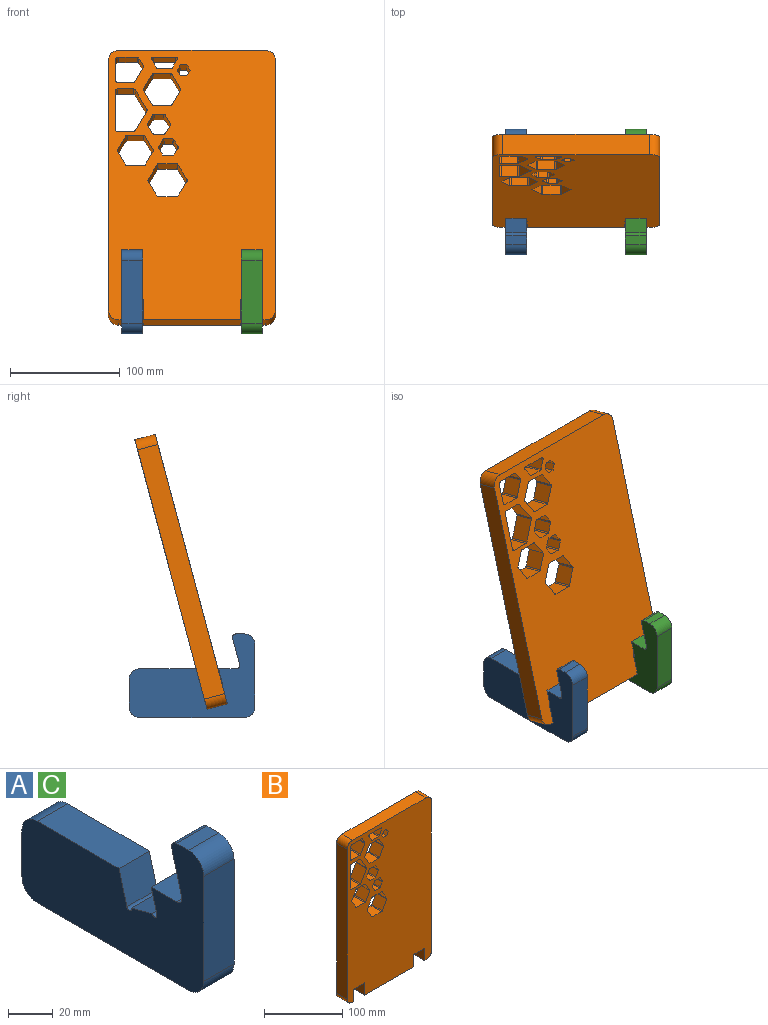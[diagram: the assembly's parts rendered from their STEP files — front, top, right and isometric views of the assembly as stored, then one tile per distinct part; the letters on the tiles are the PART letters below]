
ASSEMBLY  parts=3 mates=6
PART A: 20 faces, bbox 19.1x114.3x76.2 mm
  f0: plane 19.05x16.18mm, normal (0,0,1), area 308.3mm2, adj f7,f8,f17,f18
  f1: plane 95.25x19.05mm, normal (0,0,-1), area 1814.5mm2, adj f7,f8,f9,f12
  f2: plane 25.4x19.05mm, normal (0,1,0), area 483.9mm2, adj f7,f8,f9,f10
  f3: plane 51.51x19.05mm, normal (0,0,1), area 981.2mm2, adj f7,f8,f10,f13
  f4: plane 23.76x19.05mm, normal (0,0.97,-0.26), area 468.5mm2, adj f7,f8,f18,f19
  f5: plane 19.05x7.54mm, normal (0,0,1), area 143.7mm2, adj f7,f8,f11,f19
  f6: plane 57.15x19.05mm, normal (0,-1,0), area 1088.7mm2, adj f7,f8,f11,f12
  f7: plane 114.3x76.2mm, normal (1,0,0), area 5211.8mm2, adj f0,f1,f2,f3,f4,f5,f6,f9
  f8: plane 114.3x76.2mm, normal (-1,0,0), area 5211.8mm2, adj f0,f1,f2,f3,f4,f5,f6,f9
  f9: cylinder r=9.53mm len=19.05mm, axis (-1,0,0), area 285mm2, adj f1,f2,f7,f8
  f10: cylinder r=9.53mm len=19.05mm, axis (1,0,0), area 285mm2, adj f2,f3,f7,f8
  f11: cylinder r=9.53mm len=19.05mm, axis (1,0,0), area 285mm2, adj f5,f6,f7,f8
  f12: cylinder r=9.53mm len=19.05mm, axis (1,0,0), area 285mm2, adj f1,f6,f7,f8
  f13: plane 19.05x18.4mm, normal (0,-0.97,0.26), area 362.9mm2, adj f3,f7,f8,f14
  f14: cylinder r=1.59mm len=19.05mm, axis (-1,0,0), area 95mm2, adj f7,f8,f13,f15
  f15: plane 19.05x12.76mm, normal (0,0.26,0.97), area 251.6mm2, adj f7,f8,f14,f16
  f16: cylinder r=1.59mm len=19.05mm, axis (-1,0,0), area 95mm2, adj f7,f8,f15,f17
  f17: plane 19.05x13.34mm, normal (0,0.97,-0.26), area 263.1mm2, adj f0,f7,f8,f16
  f18: cylinder r=3.17mm len=19.05mm, axis (1,0,0), area 110.8mm2, adj f0,f4,f7,f8
  f19: cylinder r=3.17mm len=19.05mm, axis (1,0,0), area 110.8mm2, adj f4,f5,f7,f8
PART B: 115 faces, bbox 152.4x19.1x254 mm
  f0: plane 254x152.4mm, normal (0,-1,0), area 33243.4mm2, adj f2,f3,f4,f5,f6,f7,f8,f9
  f1: plane 254x152.4mm, normal (0,1,0), area 33243.4mm2, adj f2,f3,f4,f5,f6,f7,f8,f9
  f2: plane 88.9x19.05mm, normal (0,0,-1), area 1693.5mm2, adj f0,f1,f8,f15
  f3: plane 19.05x2.67mm, normal (0,0,-1), area 50.8mm2, adj f0,f1,f9,f19
  f4: plane 234.95x19.05mm, normal (-1,0,0), area 4475.8mm2, adj f0,f1,f18,f21
  f5: plane 19.05x2.67mm, normal (0,0,-1), area 50.8mm2, adj f0,f1,f14,f18
  f6: plane 234.95x19.05mm, normal (1,0,0), area 4475.8mm2, adj f0,f1,f19,f20
  f7: plane 133.35x19.05mm, normal (0,0,1), area 2540.3mm2, adj f0,f1,f20,f21
  f8: plane 19.05x19.05mm, normal (1,0,0), area 362.9mm2, adj f0,f1,f2,f12
  f9: plane 19.05x19.05mm, normal (-1,0,0), area 362.9mm2, adj f0,f1,f3,f10
  f10: cylinder r=0.79mm len=19.05mm, axis (0,-1,0), area 47.5mm2, adj f0,f1,f9,f11
  f11: plane 19.05x16.38mm, normal (0,0,-1), area 312.1mm2, adj f0,f1,f10,f12
  f12: cylinder r=0.79mm len=19.05mm, axis (0,-1,0), area 47.5mm2, adj f0,f1,f8,f11
  f13: cylinder r=0.79mm len=19.05mm, axis (0,-1,0), area 47.5mm2, adj f0,f1,f14,f17
  f14: plane 19.05x19.05mm, normal (1,0,0), area 362.9mm2, adj f0,f1,f5,f13
  f15: plane 19.05x19.05mm, normal (-1,0,0), area 362.9mm2, adj f0,f1,f2,f16
  f16: cylinder r=0.79mm len=19.05mm, axis (0,-1,0), area 47.5mm2, adj f0,f1,f15,f17
  f17: plane 19.05x16.38mm, normal (0,0,-1), area 312.1mm2, adj f0,f1,f13,f16
  f18: cylinder r=9.53mm len=19.05mm, axis (0,-1,0), area 285mm2, adj f0,f1,f4,f5
  f19: cylinder r=9.53mm len=19.05mm, axis (0,1,0), area 285mm2, adj f0,f1,f3,f6
  f20: cylinder r=9.53mm len=19.05mm, axis (0,-1,0), area 285mm2, adj f0,f1,f6,f7
  f21: cylinder r=9.53mm len=19.05mm, axis (0,1,0), area 285mm2, adj f0,f1,f4,f7
  f22: plane 19.05x16.92mm, normal (0,0,-1), area 322.4mm2, adj f0,f1,f23,f111
  f23: cylinder r=3.17mm len=19.05mm, axis (0,-1,0), area 95mm2, adj f0,f1,f22,f24
  f24: plane 19.05x18.94mm, normal (1,0,0), area 360.7mm2, adj f0,f1,f23,f114
  f25: plane 19.05x14.84mm, normal (0,0,1), area 282.8mm2, adj f0,f1,f113,f114
  f26: plane 19.05x13.44mm, normal (-0.87,0,0.5), area 295.6mm2, adj f0,f1,f112,f113
  f27: plane 19.05x7.09mm, normal (-0.87,0,-0.5), area 155.9mm2, adj f0,f1,f111,f112
  f28: plane 20.32x19.05mm, normal (0,0,-1), area 387.2mm2, adj f0,f1,f73,f76
  f29: plane 19.05x8.01mm, normal (0.87,0,0.5), area 176.1mm2, adj f0,f1,f75,f76
  f30: plane 19.05x11.08mm, normal (0,0,1), area 211mm2, adj f0,f1,f74,f75
  f31: plane 19.05x8.01mm, normal (-0.87,0,0.5), area 176.1mm2, adj f0,f1,f73,f74
  f32: plane 19.05x5.13mm, normal (0.87,0,0.5), area 112.8mm2, adj f0,f1,f33,f37
  f33: plane 19.05x5.92mm, normal (0,0,1), area 112.8mm2, adj f0,f1,f32,f34
  f34: plane 19.05x5.13mm, normal (-0.87,0,0.5), area 112.8mm2, adj f0,f1,f33,f35
  f35: plane 19.05x5.13mm, normal (-0.87,0,-0.5), area 112.8mm2, adj f0,f1,f34,f36
  f36: plane 19.05x5.92mm, normal (0,0,-1), area 112.8mm2, adj f0,f1,f35,f37
  f37: plane 19.05x5.13mm, normal (0.87,0,-0.5), area 112.8mm2, adj f0,f1,f32,f36
  f38: plane 19.05x6.4mm, normal (-0.87,0,-0.5), area 140.9mm2, adj f0,f1,f77,f82
  f39: plane 19.05x7.4mm, normal (0,0,-1), area 140.9mm2, adj f0,f1,f81,f82
  f40: plane 19.05x6.4mm, normal (0.87,0,-0.5), area 140.9mm2, adj f0,f1,f80,f81
  f41: plane 19.05x6.4mm, normal (0.87,0,0.5), area 140.9mm2, adj f0,f1,f79,f80
  f42: plane 19.05x7.4mm, normal (0,0,1), area 140.9mm2, adj f0,f1,f78,f79
  f43: plane 19.05x6.4mm, normal (-0.87,0,0.5), area 140.9mm2, adj f0,f1,f77,f78
  f44: plane 19.05x14.08mm, normal (-0.87,0,-0.5), area 309.6mm2, adj f0,f1,f83,f88
  f45: plane 19.05x16.25mm, normal (0,0,-1), area 309.6mm2, adj f0,f1,f87,f88
  f46: plane 19.05x14.08mm, normal (0.87,0,-0.5), area 309.6mm2, adj f0,f1,f86,f87
  f47: plane 19.05x14.08mm, normal (0.87,0,0.5), area 309.6mm2, adj f0,f1,f85,f86
  f48: plane 19.05x16.25mm, normal (0,0,1), area 309.6mm2, adj f0,f1,f84,f85
  f49: plane 19.05x14.08mm, normal (-0.87,0,0.5), area 309.6mm2, adj f0,f1,f83,f84
  f50: plane 36.8x19.05mm, normal (1,0,0), area 701.1mm2, adj f0,f1,f100,f104
  f51: plane 19.05x15.17mm, normal (0,0,1), area 289mm2, adj f0,f1,f103,f104
  f52: plane 19.05x18.4mm, normal (-0.87,0,0.5), area 404.8mm2, adj f0,f1,f102,f103
  f53: plane 19.05x18.4mm, normal (-0.87,0,-0.5), area 404.8mm2, adj f0,f1,f101,f102
  f54: plane 19.05x15.17mm, normal (0,0,-1), area 289mm2, adj f0,f1,f100,f101
  f55: plane 19.05x13.44mm, normal (-0.87,0,-0.5), area 295.6mm2, adj f0,f1,f105,f110
  f56: plane 19.05x15.52mm, normal (0,0,-1), area 295.6mm2, adj f0,f1,f105,f106
  f57: plane 19.05x13.44mm, normal (0.87,0,-0.5), area 295.6mm2, adj f0,f1,f106,f107
  f58: plane 19.05x13.44mm, normal (0.87,0,0.5), area 295.6mm2, adj f0,f1,f107,f108
  f59: plane 19.05x15.52mm, normal (0,0,1), area 295.6mm2, adj f0,f1,f108,f109
  f60: plane 19.05x13.44mm, normal (-0.87,0,0.5), area 295.6mm2, adj f0,f1,f109,f110
  f61: plane 19.05x7.74mm, normal (-0.87,0,-0.5), area 170.2mm2, adj f0,f1,f94,f99
  f62: plane 19.05x8.94mm, normal (0,0,-1), area 170.2mm2, adj f0,f1,f98,f99
  f63: plane 19.05x7.74mm, normal (0.87,0,-0.5), area 170.2mm2, adj f0,f1,f97,f98
  f64: plane 19.05x7.74mm, normal (0.87,0,0.5), area 170.2mm2, adj f0,f1,f96,f97
  f65: plane 19.05x8.94mm, normal (0,0,1), area 170.2mm2, adj f0,f1,f95,f96
  f66: plane 19.05x7.74mm, normal (-0.87,0,0.5), area 170.2mm2, adj f0,f1,f94,f95
  f67: plane 19.05x13.65mm, normal (-0.87,0,-0.5), area 300.1mm2, adj f0,f1,f72,f93
  f68: plane 19.05x14.84mm, normal (0,0,-1), area 282.7mm2, adj f0,f1,f92,f93
  f69: plane 19.05x12.85mm, normal (0.87,0,-0.5), area 282.7mm2, adj f0,f1,f91,f92
  f70: plane 19.05x12.85mm, normal (0.87,0,0.5), area 282.7mm2, adj f0,f1,f90,f91
  f71: plane 19.05x14.84mm, normal (0,0,1), area 282.7mm2, adj f0,f1,f89,f90
  f72: plane 19.05x13.65mm, normal (-0.87,0,0.5), area 300.1mm2, adj f0,f1,f67,f89
  f73: cylinder r=1.59mm len=19.05mm, axis (0,-1,0), area 63.3mm2, adj f0,f1,f28,f31
  f74: cylinder r=1.59mm len=19.05mm, axis (0,1,0), area 31.7mm2, adj f0,f1,f30,f31
  f75: cylinder r=1.59mm len=19.05mm, axis (0,1,0), area 31.7mm2, adj f0,f1,f29,f30
  f76: cylinder r=1.59mm len=19.05mm, axis (0,-1,0), area 63.3mm2, adj f0,f1,f28,f29
  f77: cylinder r=1.59mm len=19.05mm, axis (0,1,0), area 31.7mm2, adj f0,f1,f38,f43
  f78: cylinder r=1.59mm len=19.05mm, axis (0,1,0), area 31.7mm2, adj f0,f1,f42,f43
  f79: cylinder r=1.59mm len=19.05mm, axis (0,1,0), area 31.7mm2, adj f0,f1,f41,f42
  f80: cylinder r=1.59mm len=19.05mm, axis (0,1,0), area 31.7mm2, adj f0,f1,f40,f41
  f81: cylinder r=1.59mm len=19.05mm, axis (0,1,0), area 31.7mm2, adj f0,f1,f39,f40
  f82: cylinder r=1.59mm len=19.05mm, axis (0,1,0), area 31.7mm2, adj f0,f1,f38,f39
  f83: cylinder r=1.59mm len=19.05mm, axis (0,1,0), area 31.7mm2, adj f0,f1,f44,f49
  f84: cylinder r=1.59mm len=19.05mm, axis (0,1,0), area 31.7mm2, adj f0,f1,f48,f49
  f85: cylinder r=1.59mm len=19.05mm, axis (0,1,0), area 31.7mm2, adj f0,f1,f47,f48
  f86: cylinder r=1.59mm len=19.05mm, axis (0,1,0), area 31.7mm2, adj f0,f1,f46,f47
  f87: cylinder r=1.59mm len=19.05mm, axis (0,1,0), area 31.7mm2, adj f0,f1,f45,f46
  f88: cylinder r=1.59mm len=19.05mm, axis (0,1,0), area 31.7mm2, adj f0,f1,f44,f45
  f89: cylinder r=1.59mm len=19.05mm, axis (0,1,0), area 31.7mm2, adj f0,f1,f71,f72
  f90: cylinder r=1.59mm len=19.05mm, axis (0,1,0), area 31.7mm2, adj f0,f1,f70,f71
  f91: cylinder r=1.59mm len=19.05mm, axis (0,1,0), area 31.7mm2, adj f0,f1,f69,f70
  f92: cylinder r=1.59mm len=19.05mm, axis (0,1,0), area 31.7mm2, adj f0,f1,f68,f69
  f93: cylinder r=1.59mm len=19.05mm, axis (0,1,0), area 31.7mm2, adj f0,f1,f67,f68
  f94: cylinder r=1.59mm len=19.05mm, axis (0,1,0), area 31.7mm2, adj f0,f1,f61,f66
  f95: cylinder r=1.59mm len=19.05mm, axis (0,1,0), area 31.7mm2, adj f0,f1,f65,f66
  f96: cylinder r=1.59mm len=19.05mm, axis (0,1,0), area 31.7mm2, adj f0,f1,f64,f65
  f97: cylinder r=1.59mm len=19.05mm, axis (0,1,0), area 31.7mm2, adj f0,f1,f63,f64
  f98: cylinder r=1.59mm len=19.05mm, axis (0,1,0), area 31.7mm2, adj f0,f1,f62,f63
  f99: cylinder r=1.59mm len=19.05mm, axis (0,1,0), area 31.7mm2, adj f0,f1,f61,f62
  f100: cylinder r=1.59mm len=19.05mm, axis (0,-1,0), area 47.5mm2, adj f0,f1,f50,f54
  f101: cylinder r=1.59mm len=19.05mm, axis (0,1,0), area 31.7mm2, adj f0,f1,f53,f54
  f102: cylinder r=1.59mm len=19.05mm, axis (0,1,0), area 31.7mm2, adj f0,f1,f52,f53
  f103: cylinder r=1.59mm len=19.05mm, axis (0,1,0), area 31.7mm2, adj f0,f1,f51,f52
  f104: cylinder r=1.59mm len=19.05mm, axis (0,-1,0), area 47.5mm2, adj f0,f1,f50,f51
  f105: cylinder r=1.59mm len=19.05mm, axis (0,1,0), area 31.7mm2, adj f0,f1,f55,f56
  f106: cylinder r=1.59mm len=19.05mm, axis (0,1,0), area 31.7mm2, adj f0,f1,f56,f57
  f107: cylinder r=1.59mm len=19.05mm, axis (0,1,0), area 31.7mm2, adj f0,f1,f57,f58
  f108: cylinder r=1.59mm len=19.05mm, axis (0,1,0), area 31.7mm2, adj f0,f1,f58,f59
  f109: cylinder r=1.59mm len=19.05mm, axis (0,1,0), area 31.7mm2, adj f0,f1,f59,f60
  f110: cylinder r=1.59mm len=19.05mm, axis (0,1,0), area 31.7mm2, adj f0,f1,f55,f60
  f111: cylinder r=1.59mm len=19.05mm, axis (0,-1,0), area 31.7mm2, adj f0,f1,f22,f27
  f112: cylinder r=1.59mm len=19.05mm, axis (0,1,0), area 31.7mm2, adj f0,f1,f26,f27
  f113: cylinder r=1.59mm len=19.05mm, axis (0,1,0), area 31.7mm2, adj f0,f1,f25,f26
  f114: cylinder r=1.59mm len=19.05mm, axis (0,-1,0), area 47.5mm2, adj f0,f1,f24,f25
PART C: same geometry as A
PLACE A t=(-65.85,-0.96,-3.01)mm
PLACE B rot(axis=(-1,0,0),15deg) t=(-78.04,42.45,4.64)mm
PLACE C t=(43.12,-0.96,-3.01)mm fixed
MATE planar A.f1 <-> C.f1  axis (0,0,-1) through (-56.32,56.19,-3.01)mm
MATE planar B.f14 <-> A.f8  axis (1,0,0) through (-65.85,35.71,16.31)mm
MATE planar C.f6 <-> A.f6  axis (0,-1,0) through (52.64,-0.96,35.09)mm
MATE planar B.f1 <-> C.f13  axis (0,0.97,-0.26) through (3.64,73.81,121.71)mm
MATE planar B.f9 <-> C.f7  axis (-1,0,0) through (62.17,35.71,16.31)mm
MATE planar A.f15 <-> B.f17  axis (0,0.26,0.97) through (-56.32,37.93,25.57)mm
